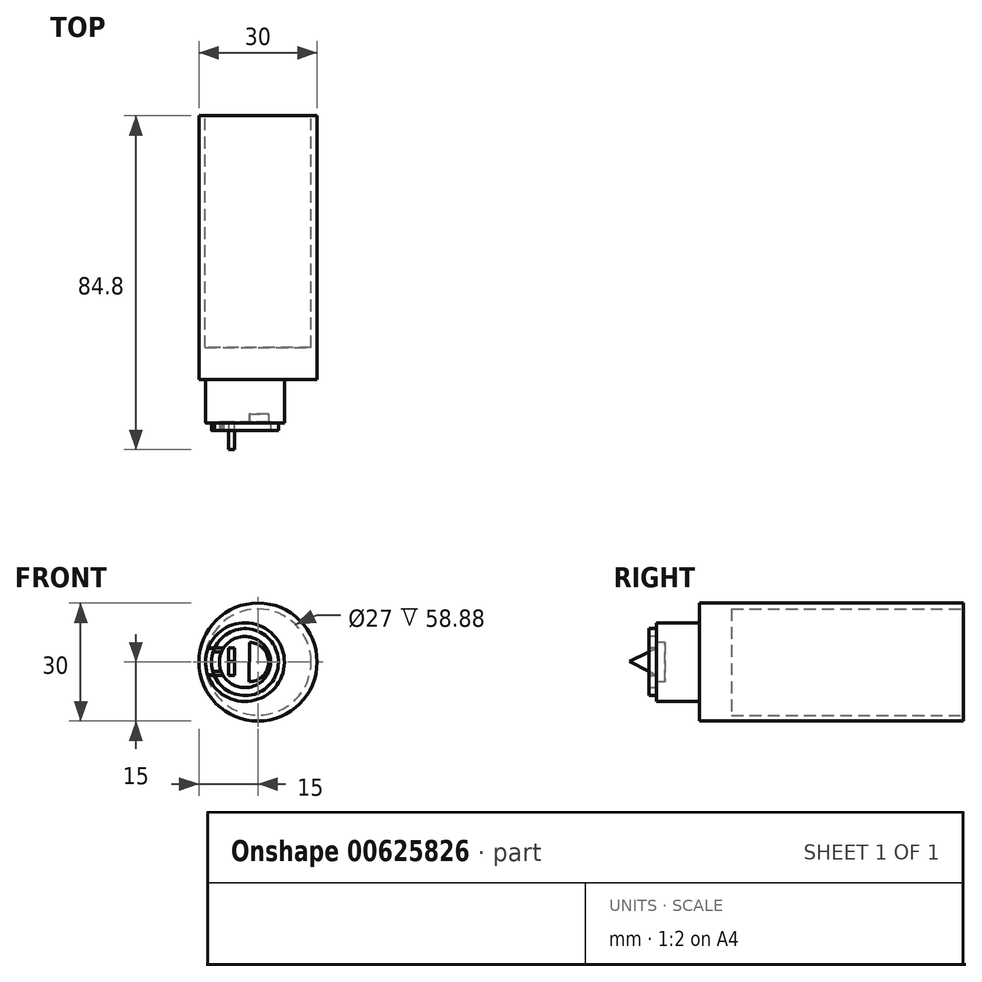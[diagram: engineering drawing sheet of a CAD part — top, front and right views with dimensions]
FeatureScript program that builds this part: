
annotation { "Feature Type Name" : "Feature", "Feature Type Description" : "" }
export const myFeature = defineFeature(function(context is Context, id is Id, definition is map)
    precondition{}
    {
        {
            var Q0;
            Q0=qCreatedBy(makeId("Front.planeOp"),FACE);
            var sketch = newSketch(context, id + "F0", { "sketchPlane" : qUnion([Q0])});
            skCircle(sketch, "E0", {"center": v(0, 0) * mm, "radius": 15 * mm});
            skSolve(sketch);
        }
        {
            var Q0;
            Q0=makeQuery(id+"F0.imprint","IMPRINT",FACE,{"disambiguationData":[TD([[makeQuery(id+"F0.imprint","IMPRINT",EDGE,{"derivedFrom":sQuery(id+"F0.wireOp",EDGE,"E0")}),1.0]])]});
            extrude(context, id + "F1", {"entities" : qUnion([Q0]), "depth" : 67 * mm, "offsetDistance" : 25 * mm});
        }
        {
            var Q0;
            Q0=makeQuery(id+"F1.opExtrude","CAP_FACE",FACE,{"disambiguationData":[OSD([sQuery(id+"F0.wireOp",EDGE,"E0")])],"isStart":false});
            var sketch = newSketch(context, id + "F2", { "sketchPlane" : qUnion([Q0])});
            skCircle(sketch, "E1", {"center": v(-3.3, 0) * mm, "radius": 10 * mm});
            skSolve(sketch);
        }
        {
            var Q0;
            Q0=makeQuery(id+"F2.imprint","IMPRINT",FACE,{"disambiguationData":[TD([[makeQuery(id+"F2.imprint","IMPRINT",EDGE,{"derivedFrom":sQuery(id+"F2.wireOp",EDGE,"E1")}),1.0]])]});
            extrude(context, id + "F3", {"entities" : qUnion([Q0]), "operationType" : NewBodyOperationType.ADD, "depth" : 11 * mm, "offsetDistance" : 25 * mm});
        }
        {
            var Q0;
            Q0=makeQuery(id+"F3.opExtrude","CAP_FACE",FACE,{"disambiguationData":[OSD([sQuery(id+"F2.wireOp",EDGE,"E1")])],"isStart":false});
            var sketch = newSketch(context, id + "F4", { "sketchPlane" : qUnion([Q0])});
            skCircle(sketch, "E2", {"center": v(-3.3, 0) * mm, "radius": 8.5 * mm});
            skSolve(sketch);
        }
        {
            var Q0;
            Q0=makeQuery(id+"F4.imprint","IMPRINT",FACE,{"disambiguationData":[TD([[makeQuery(id+"F4.imprint","IMPRINT",EDGE,{"derivedFrom":sQuery(id+"F4.wireOp",EDGE,"E2")}),1.0]])]});
            extrude(context, id + "F5", {"entities" : qUnion([Q0]), "operationType" : NewBodyOperationType.ADD, "depth" : 1.9 * mm, "offsetDistance" : 25 * mm});
        }
        {
            var Q0;
            Q0=makeQuery(id+"F5.opExtrude","CAP_FACE",FACE,{"disambiguationData":[OSD([sQuery(id+"F4.wireOp",EDGE,"E2")])],"isStart":false});
            var sketch = newSketch(context, id + "F6", { "sketchPlane" : qUnion([Q0])});
            skCircle(sketch, "E3", {"center": v(-3.3, 0) * mm, "radius": 6.5 * mm});
            skSolve(sketch);
        }
        {
            var Q0;
            Q0=makeQuery(id+"F6.imprint","IMPRINT",FACE,{"disambiguationData":[TD([[makeQuery(id+"F6.imprint","IMPRINT",EDGE,{"derivedFrom":sQuery(id+"F6.wireOp",EDGE,"E3")}),1.0]])]});
            extrude(context, id + "F7", {"entities" : qUnion([Q0]), "operationType" : NewBodyOperationType.REMOVE, "oppositeDirection" : true, "depth" : 2.1 * mm, "offsetDistance" : 25 * mm});
        }
        {
            var Q0;
            Q0=makeQuery(id+"F7.boolean.opBoolean","COPY",FACE,{"derivedFrom":makeQuery(id+"F7.opExtrude","CAP_FACE",FACE,{"disambiguationData":[OSD([sQuery(id+"F6.wireOp",EDGE,"E3")])],"isStart":false})});
            var sketch = newSketch(context, id + "F8", { "sketchPlane" : qUnion([Q0])});
            skCircle(sketch, "E4", {"center": v(-2.3, 0) * mm, "radius": 5 * mm});
            skLineSegment(sketch, "E5", {"start": v(-2.17, 5) * mm, "end": v(-2.3, -5) * mm});
            skSolve(sketch);
        }
        {
            var Q0;
            {var subQ0=sQuery(id+"F8.wireOp",EDGE,"E5");Q0=makeQuery(id+"F8.imprint","IMPRINT",FACE,{"disambiguationData":[TD([[makeQuery(id+"F8.imprint","IMPRINT",EDGE,{"derivedFrom":subQ0}),1.0]])]});}
            extrude(context, id + "F9", {"entities" : qUnion([Q0]), "operationType" : NewBodyOperationType.REMOVE, "oppositeDirection" : true, "depth" : 2 * mm, "offsetDistance" : 25 * mm});
        }
        {
            var Q0;
            Q0=makeQuery(id+"F7.boolean.opBoolean","COPY",FACE,{"derivedFrom":makeQuery(id+"F7.opExtrude","CAP_FACE",FACE,{"disambiguationData":[OSD([sQuery(id+"F6.wireOp",EDGE,"E3")])],"isStart":false})});
            var sketch = newSketch(context, id + "F10", { "sketchPlane" : qUnion([Q0])});
            skLineSegment(sketch, "E6.bottom", {"start": v(-7.43, -3.37) * mm, "end": v(-5.93, -3.37) * mm});
            skLineSegment(sketch, "E6.top", {"start": v(-7.43, 3.63) * mm, "end": v(-5.93, 3.63) * mm});
            skLineSegment(sketch, "E6.left", {"start": v(-7.43, -3.37) * mm, "end": v(-7.43, 3.63) * mm});
            skLineSegment(sketch, "E6.right", {"start": v(-5.93, -3.37) * mm, "end": v(-5.93, 3.63) * mm});
            skSolve(sketch);
        }
        {
            var Q0;
            Q0=makeQuery(id+"F10.imprint","IMPRINT",FACE,{"disambiguationData":[TD([[makeQuery(id+"F10.imprint","IMPRINT",EDGE,{"derivedFrom":sQuery(id+"F10.wireOp",EDGE,"E6.bottom")}),1.0]])]});
            extrude(context, id + "F11", {"entities" : qUnion([Q0]), "operationType" : NewBodyOperationType.ADD, "depth" : 7 * mm, "offsetDistance" : 25 * mm});
        }
        {
            var Q0;
            Q0=makeQuery(id+"F11.opExtrude","SWEPT_FACE",FACE,{"disambiguationData":[OSD([sQuery(id+"F10.wireOp",EDGE,"E6.right")])]});
            var sketch = newSketch(context, id + "F12", { "sketchPlane" : qUnion([Q0])});
            skLineSegment(sketch, "E7", {"start": v(-84.8, 0.13) * mm, "end": v(-77.8, 3.63) * mm});
            skLineSegment(sketch, "E8", {"start": v(-84.8, 0.13) * mm, "end": v(-77.8, -3.37) * mm});
            skSolve(sketch);
        }
        {
            var Q0;
            {var subQ0=sQuery(id+"F12.wireOp",EDGE,"E8");Q0=makeQuery(id+"F12.imprint","IMPRINT",FACE,{"disambiguationData":[TD([[makeQuery(id+"F12.imprint","IMPRINT",EDGE,{"derivedFrom":subQ0}),-1.0]])]});}
            extrude(context, id + "F13", {"entities" : qUnion([Q0]), "operationType" : NewBodyOperationType.REMOVE, "endBound" : BoundingType.THROUGH_ALL, "oppositeDirection" : true, "depth" : 25 * mm, "offsetDistance" : 25 * mm});
        }
        {
            var Q0;
            Q0=makeQuery(id+"F11.opExtrude","SWEPT_FACE",FACE,{"disambiguationData":[OSD([sQuery(id+"F10.wireOp",EDGE,"E6.right")])]});
            var sketch = newSketch(context, id + "F14", { "sketchPlane" : qUnion([Q0])});
            skLineSegment(sketch, "E9", {"start": v(-84.8, 0.13) * mm, "end": v(-77.8, 3.63) * mm});
            skSolve(sketch);
        }
        {
            var Q0;
            Q0=makeQuery(id+"F14.imprint","IMPRINT",FACE,{"disambiguationData":[TD([[makeQuery(id+"F14.imprint","IMPRINT",EDGE,{"derivedFrom":sQuery(id+"F14.wireOp",EDGE,"E9")}),1.0]])]});
            extrude(context, id + "F15", {"entities" : qUnion([Q0]), "operationType" : NewBodyOperationType.REMOVE, "oppositeDirection" : true, "depth" : 25 * mm, "offsetDistance" : 25 * mm});
        }
        {
            var Q0;
            Q0=makeQuery(id+"F1.opExtrude","CAP_FACE",FACE,{"disambiguationData":[OSD([sQuery(id+"F0.wireOp",EDGE,"E0")])],"isStart":true});
            var sketch = newSketch(context, id + "F16", { "sketchPlane" : qUnion([Q0])});
            skCircle(sketch, "E10", {"center": v(0, 0) * mm, "radius": 13.5 * mm});
            skSolve(sketch);
        }
        {
            var Q0;
            Q0=makeQuery(id+"F16.imprint","IMPRINT",FACE,{"disambiguationData":[TD([[makeQuery(id+"F16.imprint","IMPRINT",EDGE,{"derivedFrom":sQuery(id+"F16.wireOp",EDGE,"E10")}),1.0]])]});
            extrude(context, id + "F17", {"entities" : qUnion([Q0]), "operationType" : NewBodyOperationType.REMOVE, "oppositeDirection" : true, "depth" : 58.88 * mm, "offsetDistance" : 25 * mm});
        }
    });
